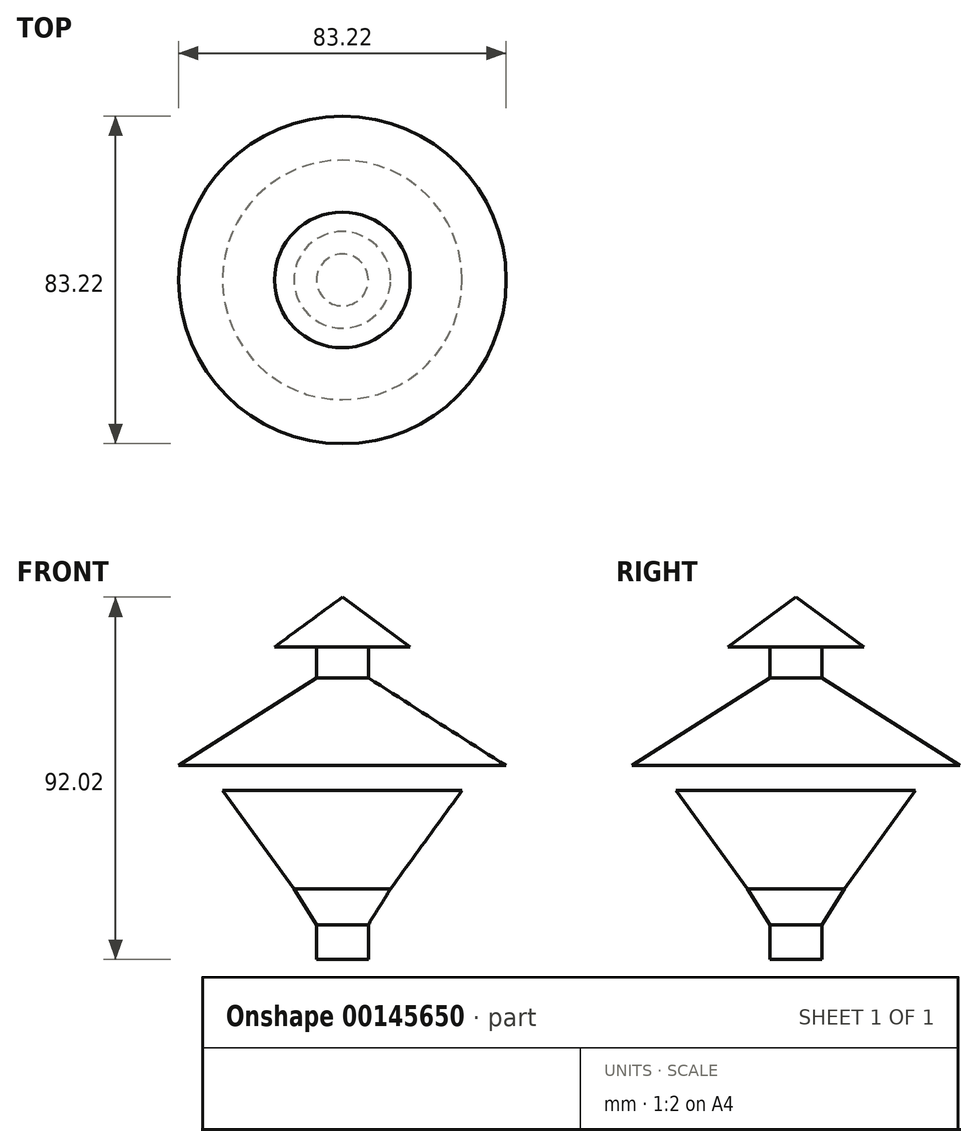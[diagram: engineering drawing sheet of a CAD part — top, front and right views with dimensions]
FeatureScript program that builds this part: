
annotation { "Feature Type Name" : "Feature", "Feature Type Description" : "" }
export const myFeature = defineFeature(function(context is Context, id is Id, definition is map)
    precondition{}
    {
        {
            var Q0;
            Q0=qCreatedBy(makeId("Front.planeOp"),FACE);
            var sketch = newSketch(context, id + "F0", { "sketchPlane" : qUnion([Q0])});
            skLineSegment(sketch, "E0", {"start": v(0, 0) * mm, "end": v(0, 42.8) * mm, "construction": true});
            skLineSegment(sketch, "E1", {"start": v(0, 42.8) * mm, "end": v(17.23, 30.15) * mm});
            skLineSegment(sketch, "E2", {"start": v(17.23, 30.15) * mm, "end": v(6.6, 30.15) * mm});
            skLineSegment(sketch, "E3", {"start": v(6.6, 30.15) * mm, "end": v(6.6, 22.27) * mm});
            skLineSegment(sketch, "E4", {"start": v(6.6, 22.27) * mm, "end": v(41.6, 0) * mm});
            skLineSegment(sketch, "E5.MirrorCS", {"start": v(-17.23, 30.15) * mm, "end": v(-6.6, 30.15) * mm});
            skLineSegment(sketch, "E6.MirrorCS", {"start": v(-6.6, 22.27) * mm, "end": v(-41.6, 0) * mm});
            skLineSegment(sketch, "E7.MirrorCS", {"start": v(-6.6, 30.15) * mm, "end": v(-6.6, 22.27) * mm});
            skLineSegment(sketch, "E8.MirrorCS", {"start": v(0, 42.8) * mm, "end": v(-17.23, 30.15) * mm});
            skSolve(sketch);
        }
        {
            var Q0;
            Q0=sQuery(id+"F0.wireOp",EDGE,"E1");
            var Q1;
            Q1=sQuery(id+"F0.wireOp",EDGE,"E2");
            var Q2;
            Q2=sQuery(id+"F0.wireOp",EDGE,"E3");
            var Q3;
            Q3=sQuery(id+"F0.wireOp",EDGE,"E4");
            var Q4;
            Q4=sQuery(id+"F0.wireOp",EDGE,"E0");
            revolve(context, id + "F1", {"bodyType" : ToolBodyType.SURFACE, "surfaceEntities" : qUnion([Q0, Q1, Q2, Q3]), "axis" : qUnion([Q4]), "revolveType" : RevolveType.FULL});
        }
        {
            var Q0;
            Q0=qCreatedBy(makeId("Front.planeOp"),FACE);
            var sketch = newSketch(context, id + "F2", { "sketchPlane" : qUnion([Q0])});
            skLineSegment(sketch, "E9", {"start": v(0, -49.03) * mm, "end": v(0, -6.32) * mm, "construction": true});
            skLineSegment(sketch, "E10", {"start": v(30.43, -6.32) * mm, "end": v(12.28, -31.25) * mm});
            skLineSegment(sketch, "E11", {"start": v(12.28, -31.25) * mm, "end": v(6.6, -40.42) * mm});
            skLineSegment(sketch, "E12", {"start": v(6.6, -40.42) * mm, "end": v(6.6, -49.22) * mm});
            skLineSegment(sketch, "E13.MirrorCS", {"start": v(-30.43, -6.32) * mm, "end": v(-12.28, -31.25) * mm});
            skLineSegment(sketch, "E14.MirrorCS", {"start": v(-6.6, -40.42) * mm, "end": v(-6.6, -49.22) * mm});
            skLineSegment(sketch, "E15.MirrorCS", {"start": v(-12.28, -31.25) * mm, "end": v(-6.6, -40.42) * mm});
            skSolve(sketch);
        }
        {
            var Q0;
            Q0=sQuery(id+"F2.wireOp",EDGE,"E10");
            var Q1;
            Q1=sQuery(id+"F2.wireOp",EDGE,"E11");
            var Q2;
            Q2=sQuery(id+"F2.wireOp",EDGE,"E12");
            var Q3;
            Q3=sQuery(id+"F2.wireOp",EDGE,"E9");
            revolve(context, id + "F3", {"bodyType" : ToolBodyType.SURFACE, "surfaceEntities" : qUnion([Q0, Q1, Q2]), "axis" : qUnion([Q3]), "revolveType" : RevolveType.FULL});
        }
    });
